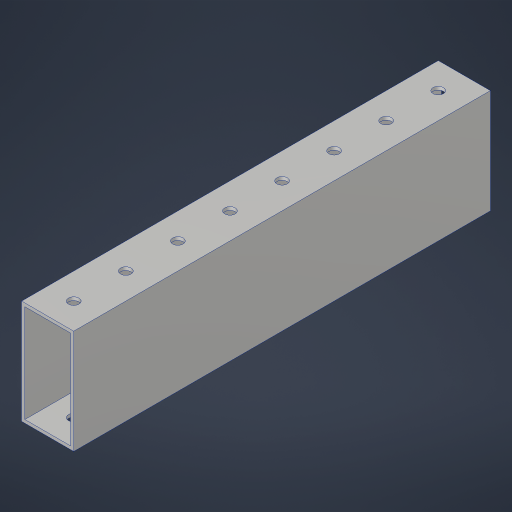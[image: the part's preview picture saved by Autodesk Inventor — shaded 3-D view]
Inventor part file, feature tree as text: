
AUTODESK INVENTOR PART (.ipt)
format: ipt  version: 2023.4 (Build 274418000, 418)  size: 193,536 bytes
history: native  units: in
note: dims shown in document units (in); Inventor stores cm internally (conversion verified against a paired STEP export)
features: extrude x2, sketch x2, projected_geometry x2, hole x1, pattern_linear x1
ambient origin geometry x8: Origin, YZ Plane, XZ Plane, XY Plane, X Axis, Y Axis, Z Axis, Center Point
bodies: Solid1 (feature_tree)
feature tree (8):
  extrude  "Extrusion1"  TaperAngle=45.0deg  [1 undecoded]
  extrude  "Extrusion4"  Depth=1.0in
  hole  "Hole1"  [1 undecoded]
  pattern_linear  "Rectangular Pattern1"  [2 undecoded]
  sketch  "Sketch4"  dims[d4=0.0in d13=45.0deg]
  sketch  "Sketch5"  dims[d14=0.0in d15=0.0in d16=0.5in d17=0.201in d18=0.75in d19=0.385in d20=0.25in d21=0.5635in d22=1.0in d23=0.8108in d24=3.1496in d26=1.0in]
  projected_geometry  "Project Cut Edges1"
  projected_geometry  "Project Cut Edges2"
note: 4 required parameter values undecoded (feature->parameter linkage not recoverable at this tier; creation-order binding heuristic only, values carry confidence <= 0.55)
